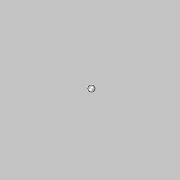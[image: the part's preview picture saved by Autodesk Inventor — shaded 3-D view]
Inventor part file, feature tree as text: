
AUTODESK INVENTOR PART (.ipt)
format: ipt  version: 2017 (Build 210142000, 142)  size: 103,936 bytes
history: native  units: mm
features: other x26, extrude x2, sketch x2, mirror x1, pattern_linear x1
ambient origin geometry x7: Origin, YZ Plane, XZ Plane, X Axis, Y Axis, Z Axis, Center Point
bodies: Solid1 (feature_tree)
feature tree (32):
  other  "Table"
  other  "CableLadderKHJZP-150x3000"
  other  "CableLadderKHJZP-200x3000"
  other  "CableLadderKHJZP-300x3000"
  other  "CableLadderKHJZP-400x3000"
  other  "CableLadderKHJZP-500x3000"
  other  "CableLadderKHJZP-600x3000"
  other  "CableLadderKHJZP-800x3000"
  other  "CableLadderKHJZP-1000x3000"
  other  "CableLadderKHJZP-150x4000"
  other  "CableLadderKHJZP-200x4000"
  other  "CableLadderKHJZP-300x4000"
  other  "CableLadderKHJZP-400x4000"
  other  "CableLadderKHJZP-500x4000"
  other  "CableLadderKHJZP-600x4000"
  other  "CableLadderKHJZP-800x4000"
  other  "CableLadderKHJZP-1000x4000"
  other  "CableLadderKHJZP-150x6000"
  other  "CableLadderKHJZP-200x6000"
  other  "CableLadderKHJZP-300x6000"
  other  "CableLadderKHJZP-400x6000"
  other  "CableLadderKHJZP-500x6000"
  other  "CableLadderKHJZP-600x6000"
  other  "CableLadderKHJZP-800x6000"
  other  "CableLadderKHJZP-1000x6000"
  extrude  "Extrusion1"  Depth=18.0mm
  mirror  "Mirror1"
  extrude  "Extrusion2"  Depth=30.0mm
  pattern_linear  "Rectangular Pattern1"  Spacing1=18.0mm  [1 undecoded]
  other  "XY Ground Plane"
  sketch  "Sketch4"  dims[d0=55.0mm d1=18.0mm]
  sketch  "Sketch5"  dims[d4=0.0mm d5=30.0mm d6=18.0mm d7=3000.0mm d8=0.0mm d9=125.0mm d10=120.0mm d12=250.0mm d13=0.0mm]
note: 1 required parameter value undecoded (feature->parameter linkage not recoverable at this tier; creation-order binding heuristic only, values carry confidence <= 0.55)
